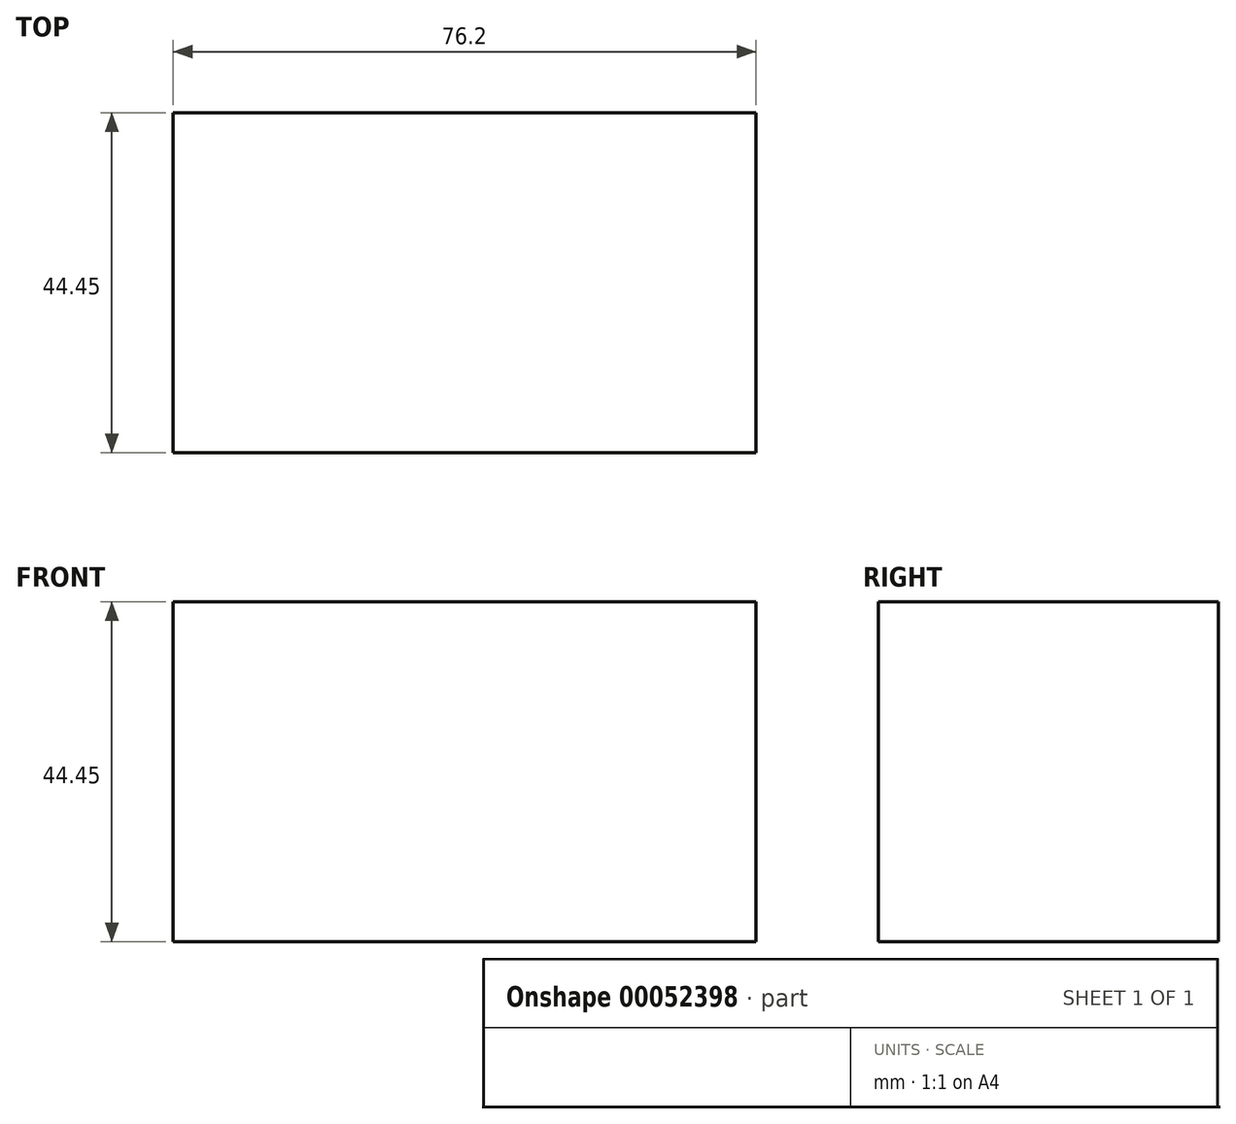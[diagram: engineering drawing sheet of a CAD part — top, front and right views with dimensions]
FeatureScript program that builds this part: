
annotation { "Feature Type Name" : "Feature", "Feature Type Description" : "" }
export const myFeature = defineFeature(function(context is Context, id is Id, definition is map)
    precondition{}
    {
        {
            var Q0;
            Q0=qCreatedBy(makeId("Right.planeOp"),FACE);
            var sketch = newSketch(context, id + "F0", { "sketchPlane" : qUnion([Q0])});
            skLineSegment(sketch, "E0.bottom", {"start": v(0, 0) * mm, "end": v(-44.45, 0) * mm});
            skLineSegment(sketch, "E0.top", {"start": v(0, 44.45) * mm, "end": v(-44.45, 44.45) * mm});
            skLineSegment(sketch, "E0.left", {"start": v(0, 0) * mm, "end": v(0, 44.45) * mm});
            skLineSegment(sketch, "E0.right", {"start": v(-44.45, 0) * mm, "end": v(-44.45, 44.45) * mm});
            skSolve(sketch);
        }
        {
            var Q0;
            Q0 = qSketchRegion(id + "F0", true);
            extrude(context, id + "F1", {"entities" : qUnion([Q0]), "depth" : 25.4 * mm});
        }
        {
            var Q0;
            Q0 = qSketchRegion(id + "F0", true);
            extrude(context, id + "F2", {"entities" : qUnion([Q0]), "operationType" : NewBodyOperationType.ADD, "depth" : 25.4 * mm});
        }
        {
            var Q0;
            Q0=makeQuery(id+"F1.opExtrude","CAP_FACE",FACE,{"disambiguationData":[OSD([sQuery(id+"F0.wireOp",EDGE,"E0.bottom"),sQuery(id+"F0.wireOp",EDGE,"E0.top"),sQuery(id+"F0.wireOp",EDGE,"E0.left"),sQuery(id+"F0.wireOp",EDGE,"E0.right")])],"isStart":false});
            extrude(context, id + "F3", {"entities" : qUnion([Q0]), "operationType" : NewBodyOperationType.ADD, "oppositeDirection" : true, "depth" : 76.2 * mm});
        }
        {
            var Q0;
            {var subQ0=sQuery(id+"F0.wireOp",EDGE,"E0.top");Q0=makeQuery(id+"F3.boolean.opBoolean","MERGE",FACE,{"derivedFrom":[makeQuery(id+"F1.opExtrude","SWEPT_FACE",FACE,{"disambiguationData":[OSD([subQ0])]}),makeQuery(id+"F3.opExtrude","SWEPT_FACE",FACE,{"disambiguationData":[OSD([subQ0])]})]});}
            var sketch = newSketch(context, id + "F4", { "sketchPlane" : qUnion([Q0])});
            skPoint(sketch, "E1", {"position": v(-19.05, -44.45) * mm});
            skSolve(sketch);
        }
    });
